# Revit family: PRD_FrankeWS_SoapDshs_SoapTray_BS648
name_source: partatom
category: Furniture
revit_build: Autodesk Revit 2018 (Build: 20190510_1515(x64)
units: mm (PartAtom-declared; Revit-internal decimal feet)

## family parameters
Cut with Voids When Loaded = No
Host = Face
OmniClass Number = 23.40.20.21
OmniClass Title = Toilet and Bath Specialties
Room Calculation Point = No
Shared = No

## types (1)
- BS648
    AssetType = Fixed
    BIMObjectName = PRD_AR_SoapDishes_SoapTray_BS648
    Category = Pr_40_20_76_82, Soap dishes
    Color = Stainless steel
    Default Elevation = 1100 mm
    Description = Tray/shelf for wall mounting, stainless steel, surface satin finished, material thickness 0.8 mm, drilling holes for water drain, incl. stainless steel screws and dowels.
    DurationUnit = year
    Features = stainless steel, 0.80 mm, satin finished, wall mounting, 195x77x96 mm (WxHxD)
    Finish = Satin finished
    FinishAndColour = Stainless steel, satin finished
    Form = Wall mounted
    IfcExportAs = IfcFurnitureType
    IfcExportType = NOTDEFINED
    IntegralAccessories = Stainless steel screws and dowels incl.
    MainColor = Stainless steel
    Manufacturer = KWC Group AG
    ManufacturerName = KWC Group AG
    ManufacturerURL = www.kwc.com
    Material = Stainless steel
    Materials = Stainless steel 1.4301
    Model = BS648
    ModelNumber = 2000057041
    ModelReference = BS648
    NBSDescription = Soap dishes
    NBSReference = 45-35-72/356
    Name = Soap tray BS648
    NominalDepth = 96 mm  [stored 0.314961 ft]
    NominalHeight = 77 mm  [stored 0.252625 ft]
    NominalLength = 195 mm  [stored 0.639764 ft]
    NominalWidth = 195 mm  [stored 0.639764 ft]
    ProductInformation = https://pim.kwc.com
    Size = 195 x 77 x 96 mm
    Style = Soap tray
    TrayMaterial = PRD_AR_StainlessSteel_SatinFinished
    URL = www.kwc.com
    Uniclass2015Code = Pr_40_20_76_82
    Uniclass2015Title = Soap dishes
    Uniclass2015Version = Products v1.5
    Version = 1
    WarrantyDurationUnit = year

note: [stored X ft] marks values corroborated as IEEE doubles in the binary element streams (Revit-internal decimal feet)

## geometry (parser evidence)
native form markers: Sweep x2
no freeform markers — native parametric forms only
